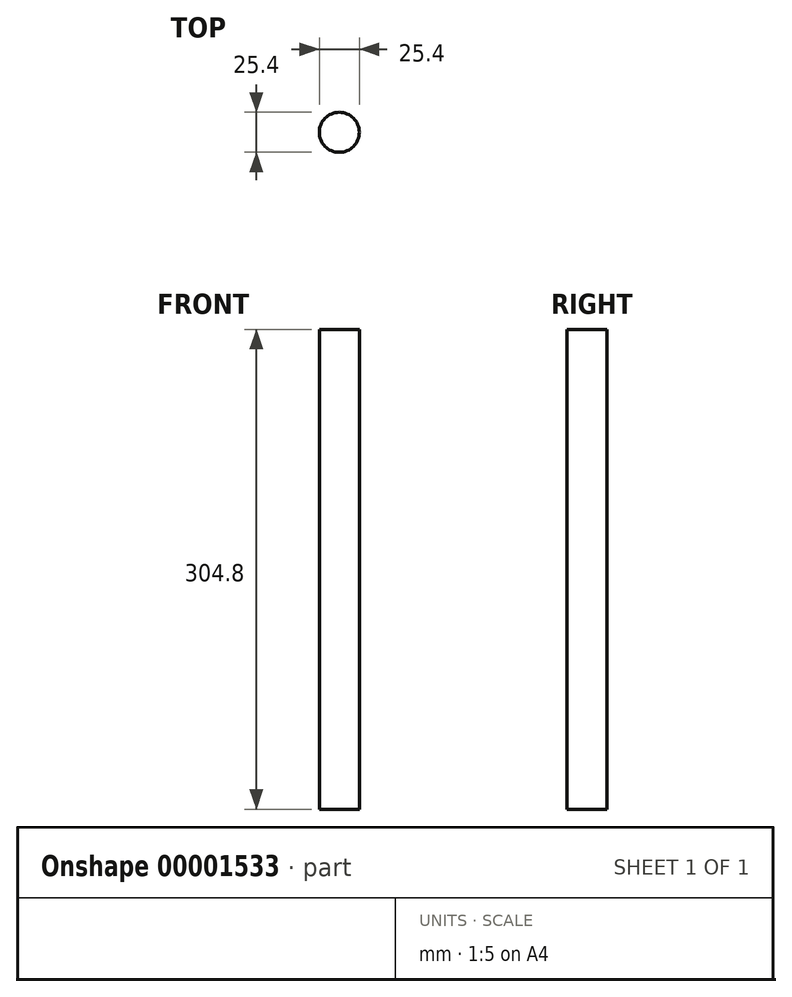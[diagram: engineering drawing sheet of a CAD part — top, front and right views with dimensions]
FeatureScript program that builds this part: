
annotation { "Feature Type Name" : "Feature", "Feature Type Description" : "" }
export const myFeature = defineFeature(function(context is Context, id is Id, definition is map)
    precondition{}
    {
        {
            var Q0;
            Q0=qCreatedBy(makeId("Top.planeOp"),FACE);
            var sketch = newSketch(context, id + "F0", { "sketchPlane" : qUnion([Q0])});
            skCircle(sketch, "E0", {"center": v(0, 0) * mm, "radius": 12.7 * mm});
            skSolve(sketch);
        }
        {
            var Q0;
            Q0=makeQuery(id+"F0.imprint","IMPRINT",FACE,{"disambiguationData":[TD([[makeQuery(id+"F0.imprint","IMPRINT",EDGE,{"derivedFrom":sQuery(id+"F0.wireOp",EDGE,"E0")}),1.0]])]});
            extrude(context, id + "F1", {"entities" : qUnion([Q0]), "depth" : 304.8 * mm});
        }
    });
